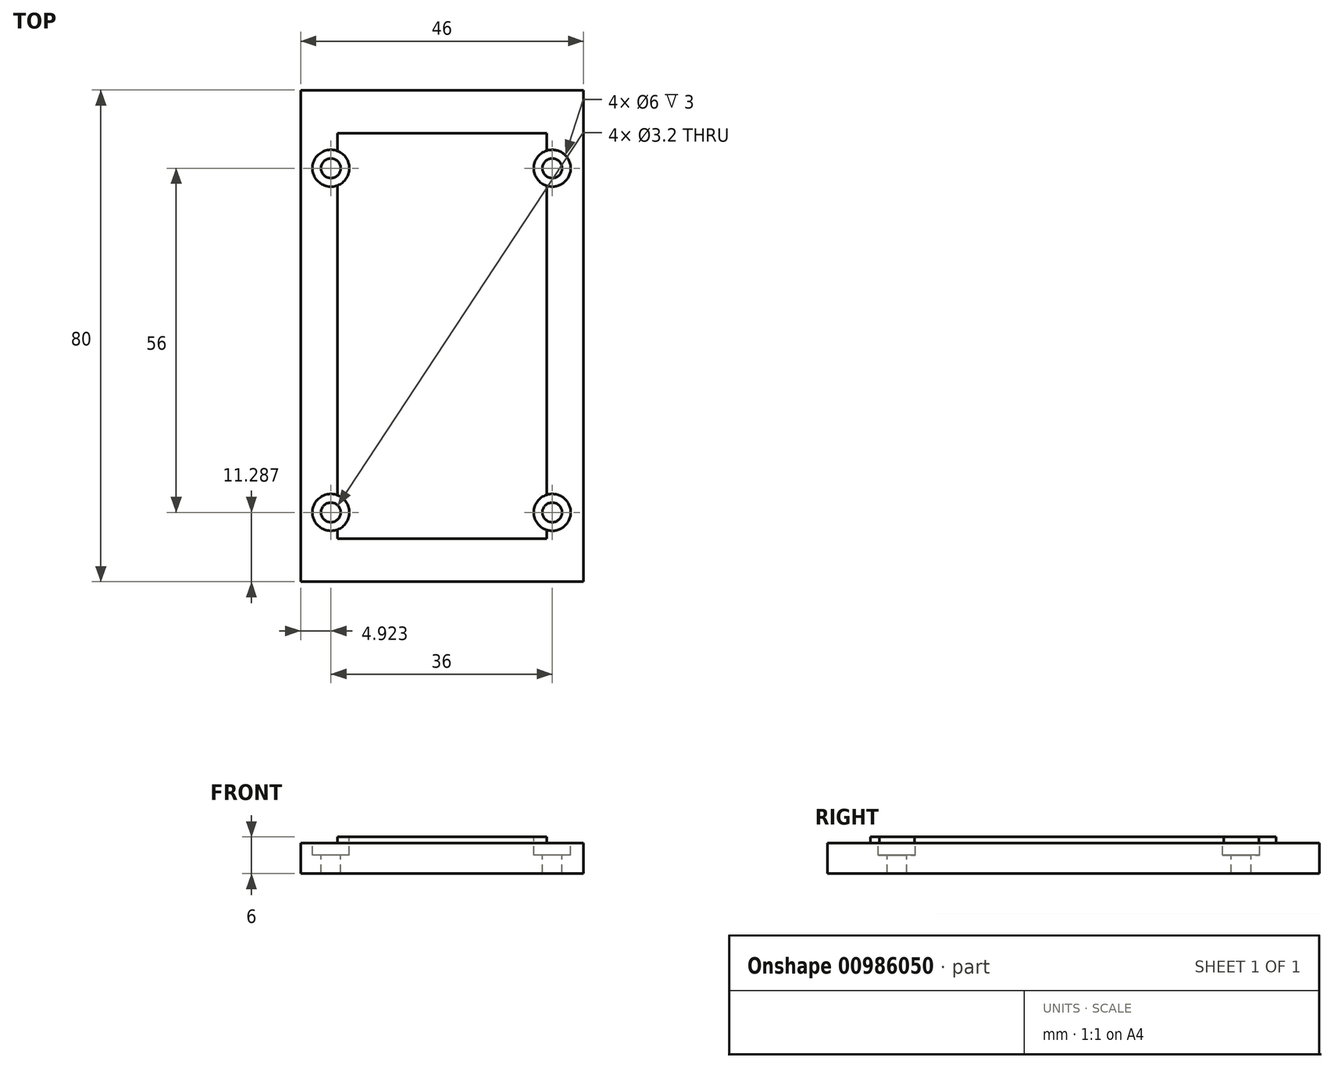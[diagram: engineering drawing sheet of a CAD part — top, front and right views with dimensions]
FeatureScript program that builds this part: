
annotation { "Feature Type Name" : "Feature", "Feature Type Description" : "" }
export const myFeature = defineFeature(function(context is Context, id is Id, definition is map)
    precondition{}
    {
        {
            var Q0;
            Q0=qCreatedBy(makeId("Top.planeOp"),FACE);
            var sketch = newSketch(context, id + "F0", { "sketchPlane" : qUnion([Q0])});
            skLineSegment(sketch, "E0.bottom", {"start": v(-24.26, 40.97) * mm, "end": v(21.74, 40.97) * mm});
            skLineSegment(sketch, "E0.top", {"start": v(-24.26, -39.03) * mm, "end": v(21.74, -39.03) * mm});
            skLineSegment(sketch, "E0.left", {"start": v(-24.26, 40.97) * mm, "end": v(-24.26, -39.03) * mm});
            skLineSegment(sketch, "E0.right", {"start": v(21.74, 40.97) * mm, "end": v(21.74, -39.03) * mm});
            skLineSegment(sketch, "E1.bottom", {"start": v(-18.26, 33.97) * mm, "end": v(15.74, 33.97) * mm, "construction": true});
            skLineSegment(sketch, "E1.top", {"start": v(-18.26, -32.03) * mm, "end": v(15.74, -32.03) * mm, "construction": true});
            skLineSegment(sketch, "E1.left", {"start": v(-18.26, 33.97) * mm, "end": v(-18.26, -32.03) * mm, "construction": true});
            skLineSegment(sketch, "E1.right", {"start": v(15.74, 33.97) * mm, "end": v(15.74, -32.03) * mm, "construction": true});
            skCircle(sketch, "E2", {"center": v(16.66, -27.74) * mm, "radius": 1.6 * mm, "construction": true});
            skCircle(sketch, "E3", {"center": v(16.66, -27.74) * mm, "radius": 3 * mm, "construction": true});
            skCircle(sketch, "E4", {"center": v(-19.34, 28.26) * mm, "radius": 1.6 * mm, "construction": true});
            skCircle(sketch, "E5", {"center": v(-19.34, 28.26) * mm, "radius": 3 * mm, "construction": true});
            skCircle(sketch, "E6", {"center": v(16.66, 28.26) * mm, "radius": 1.6 * mm, "construction": true});
            skCircle(sketch, "E7", {"center": v(16.66, 28.26) * mm, "radius": 3 * mm, "construction": true});
            skCircle(sketch, "E8", {"center": v(-19.34, -27.74) * mm, "radius": 1.6 * mm, "construction": true});
            skCircle(sketch, "E9", {"center": v(-19.34, -27.74) * mm, "radius": 3 * mm, "construction": true});
            skSolve(sketch);
        }
        {
            var Q0;
            Q0 = qSketchRegion(id + "F0", true);
            extrude(context, id + "F1", {"entities" : qUnion([Q0]), "depth" : 5 * mm, "offsetDistance" : 25 * mm});
        }
        {
            var Q0;
            Q0=makeQuery(id+"F1.opExtrude","CAP_FACE",FACE,{"disambiguationData":[OSD([sQuery(id+"F0.wireOp",EDGE,"E0.bottom"),sQuery(id+"F0.wireOp",EDGE,"E0.top"),sQuery(id+"F0.wireOp",EDGE,"E0.left"),sQuery(id+"F0.wireOp",EDGE,"E0.right")])],"isStart":false});
            var sketch = newSketch(context, id + "F2", { "sketchPlane" : qUnion([Q0])});
            skLineSegment(sketch, "E10.0", {"start": v(-18.26, 33.97) * mm, "end": v(15.74, 33.97) * mm});
            skLineSegment(sketch, "E11.0", {"start": v(-18.26, 33.97) * mm, "end": v(-18.26, -32.03) * mm});
            skLineSegment(sketch, "E12.0", {"start": v(15.74, 33.97) * mm, "end": v(15.74, -32.03) * mm});
            skLineSegment(sketch, "E13.0", {"start": v(-18.26, -32.03) * mm, "end": v(15.74, -32.03) * mm});
            skSolve(sketch);
        }
        {
            var Q0;
            Q0 = qSketchRegion(id + "F2", true);
            extrude(context, id + "F3", {"entities" : qUnion([Q0]), "operationType" : NewBodyOperationType.ADD, "depth" : 1 * mm, "offsetDistance" : 25 * mm});
        }
        {
            var Q0;
            Q0=makeQuery(id+"F3.opExtrude","CAP_FACE",FACE,{"disambiguationData":[OSD([sQuery(id+"F2.wireOp",EDGE,"E10.0"),sQuery(id+"F2.wireOp",EDGE,"E11.0"),sQuery(id+"F2.wireOp",EDGE,"E12.0"),sQuery(id+"F2.wireOp",EDGE,"E13.0")])],"isStart":false});
            var sketch = newSketch(context, id + "F4", { "sketchPlane" : qUnion([Q0])});
            skCircle(sketch, "E14.0", {"center": v(-19.34, 28.26) * mm, "radius": 3 * mm});
            skCircle(sketch, "E15.0", {"center": v(16.66, 28.26) * mm, "radius": 3 * mm});
            skCircle(sketch, "E16.0", {"center": v(-19.34, -27.74) * mm, "radius": 3 * mm});
            skCircle(sketch, "E17.0", {"center": v(16.66, -27.74) * mm, "radius": 3 * mm});
            skSolve(sketch);
        }
        {
            var Q0;
            Q0 = qSketchRegion(id + "F4", true);
            extrude(context, id + "F5", {"entities" : qUnion([Q0]), "operationType" : NewBodyOperationType.REMOVE, "oppositeDirection" : true, "depth" : 3 * mm, "offsetDistance" : 25 * mm});
        }
        {
            var Q0;
            Q0=makeQuery(id+"F3.opExtrude","CAP_FACE",FACE,{"disambiguationData":[OSD([sQuery(id+"F2.wireOp",EDGE,"E10.0"),sQuery(id+"F2.wireOp",EDGE,"E11.0"),sQuery(id+"F2.wireOp",EDGE,"E12.0"),sQuery(id+"F2.wireOp",EDGE,"E13.0")])],"isStart":false});
            var sketch = newSketch(context, id + "F6", { "sketchPlane" : qUnion([Q0])});
            skCircle(sketch, "E18.0", {"center": v(-19.34, 28.26) * mm, "radius": 1.6 * mm});
            skCircle(sketch, "E19.0", {"center": v(16.66, 28.26) * mm, "radius": 1.6 * mm});
            skCircle(sketch, "E20.0", {"center": v(-19.34, -27.74) * mm, "radius": 1.6 * mm});
            skCircle(sketch, "E21.0", {"center": v(16.66, -27.74) * mm, "radius": 1.6 * mm});
            skSolve(sketch);
        }
        {
            var Q0;
            Q0 = qSketchRegion(id + "F6", true);
            extrude(context, id + "F7", {"entities" : qUnion([Q0]), "operationType" : NewBodyOperationType.REMOVE, "endBound" : BoundingType.THROUGH_ALL, "oppositeDirection" : true, "depth" : 25 * mm, "offsetDistance" : 25 * mm});
        }
    });
